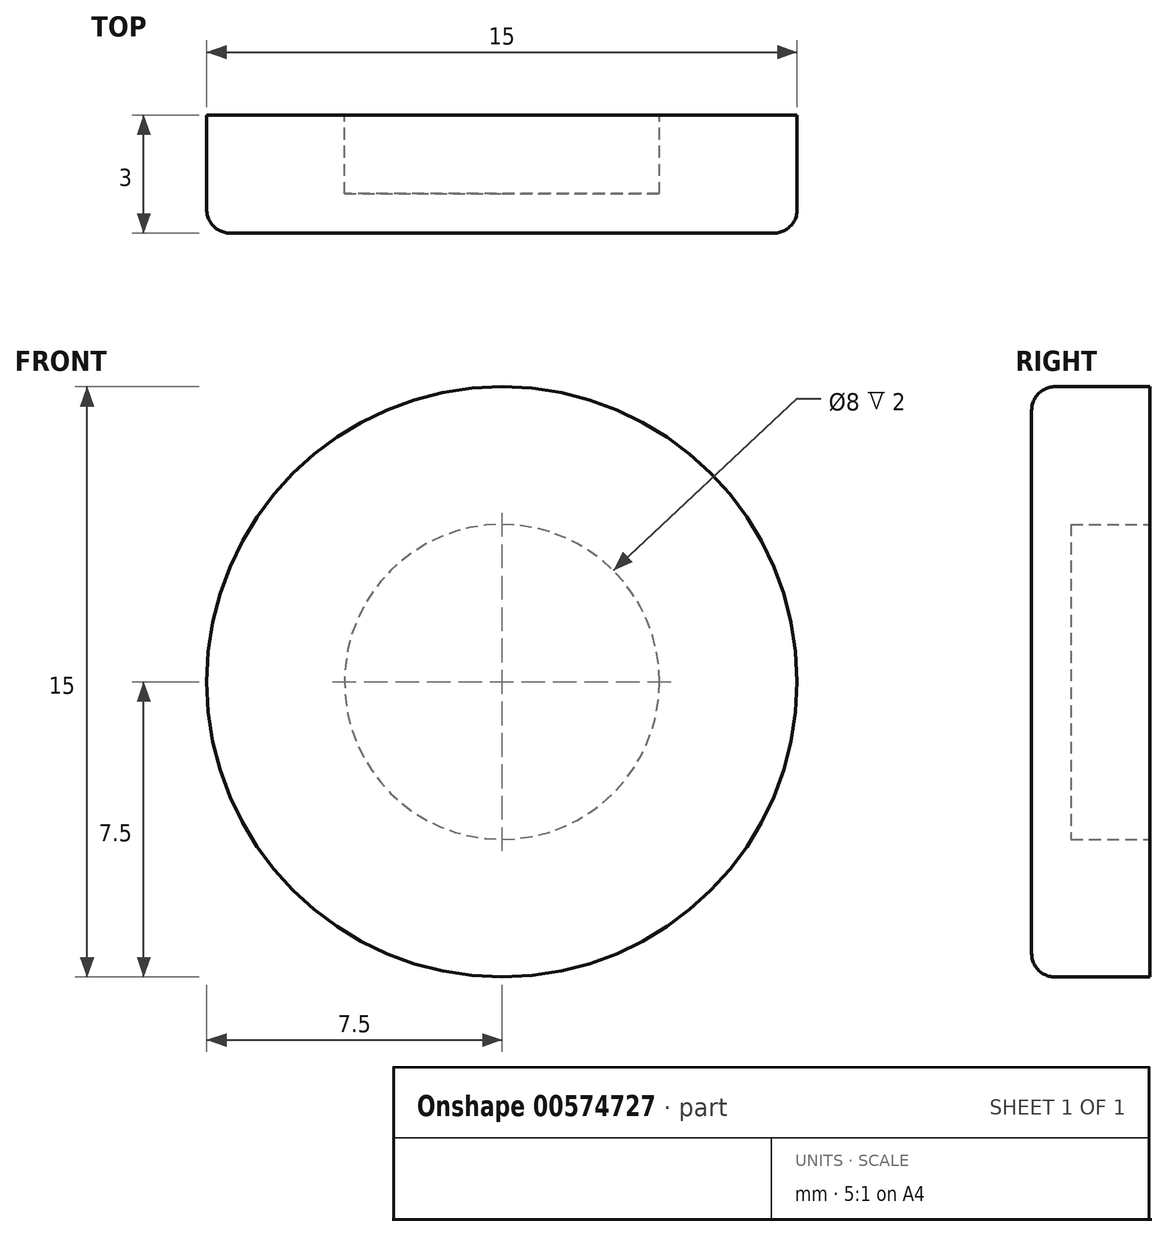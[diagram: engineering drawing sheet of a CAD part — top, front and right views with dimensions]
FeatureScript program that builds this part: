
annotation { "Feature Type Name" : "Feature", "Feature Type Description" : "" }
export const myFeature = defineFeature(function(context is Context, id is Id, definition is map)
    precondition{}
    {
        {
            var Q0;
            Q0=qCreatedBy(makeId("Front.planeOp"),FACE);
            var sketch = newSketch(context, id + "F0", { "sketchPlane" : qUnion([Q0])});
            skCircle(sketch, "E0", {"center": v(0, 0) * mm, "radius": 7.5 * mm});
            skSolve(sketch);
        }
        {
            var Q0;
            Q0=makeQuery(id+"F0.imprint","IMPRINT",FACE,{"disambiguationData":[TD([[makeQuery(id+"F0.imprint","IMPRINT",EDGE,{"derivedFrom":sQuery(id+"F0.wireOp",EDGE,"E0")}),1.0]])]});
            extrude(context, id + "F1", {"entities" : qUnion([Q0]), "depth" : 3 * mm, "offsetDistance" : 25 * mm});
        }
        {
            var Q0;
            Q0=makeQuery(id+"F1.opExtrude","CAP_EDGE",EDGE,{"disambiguationData":[OSD([sQuery(id+"F0.wireOp",EDGE,"E0")])],"isStart":false});
            fillet(context, id + "F2", {"entities" : qUnion([Q0]), "radius" : 0.6 * mm, "tangentPropagation" : true, "allowEdgeOverflow" : false});
        }
        {
            var Q0;
            Q0=makeQuery(id+"F1.opExtrude","CAP_FACE",FACE,{"disambiguationData":[OSD([sQuery(id+"F0.wireOp",EDGE,"E0")])],"isStart":true});
            var sketch = newSketch(context, id + "F3", { "sketchPlane" : qUnion([Q0])});
            skCircle(sketch, "E1", {"center": v(0, 0) * mm, "radius": 4 * mm});
            skSolve(sketch);
        }
        {
            var Q0;
            Q0=makeQuery(id+"F3.imprint","IMPRINT",FACE,{"disambiguationData":[TD([[makeQuery(id+"F3.imprint","IMPRINT",EDGE,{"derivedFrom":sQuery(id+"F3.wireOp",EDGE,"E1")}),1.0]])]});
            extrude(context, id + "F4", {"entities" : qUnion([Q0]), "operationType" : NewBodyOperationType.REMOVE, "oppositeDirection" : true, "depth" : 2 * mm, "offsetDistance" : 25 * mm});
        }
    });
